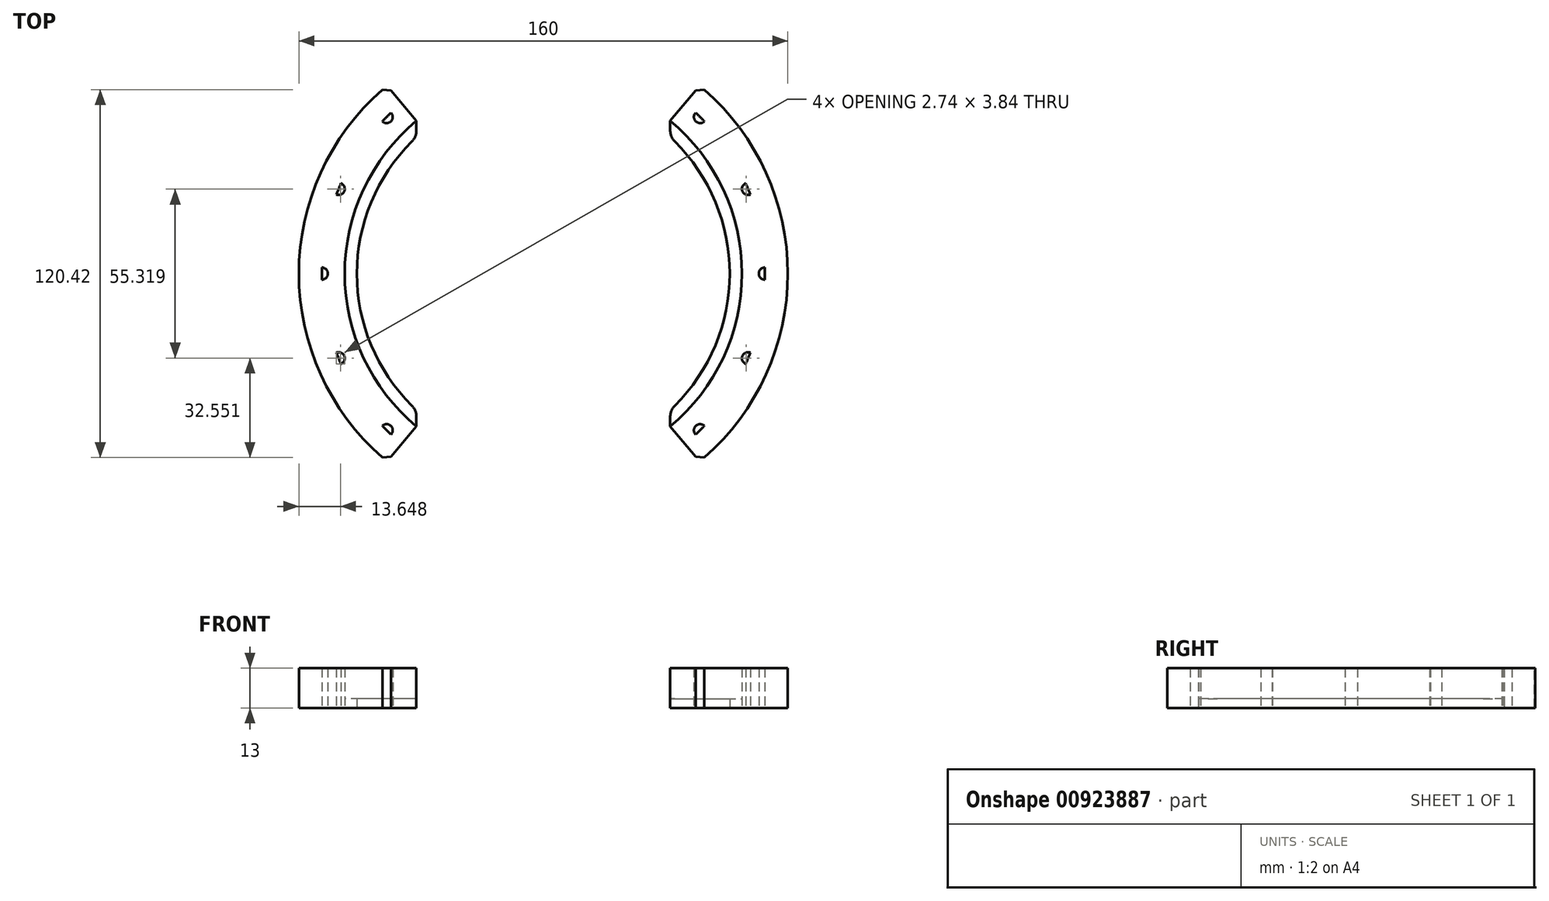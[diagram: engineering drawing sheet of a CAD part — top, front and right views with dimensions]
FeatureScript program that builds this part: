
annotation { "Feature Type Name" : "Feature", "Feature Type Description" : "" }
export const myFeature = defineFeature(function(context is Context, id is Id, definition is map)
    precondition{}
    {
        {
            var Q0;
            Q0=qCreatedBy(makeId("Top.planeOp"),FACE);
            var sketch = newSketch(context, id + "F0", { "sketchPlane" : qUnion([Q0])});
            skArc(sketch, "E0", {"start": v(-55.64, 25) * mm, "mid": v(-61, 0) * mm, "end": v(-55.64, -25) * mm});
            skArc(sketch, "E1.trimOffspring", {"start": v(55.64, -25) * mm, "mid": v(61, 0) * mm, "end": v(55.64, 25) * mm});
            skCircle(sketch, "E2", {"center": v(0, 0) * mm, "radius": 61 * mm});
            skCircle(sketch, "E3", {"center": v(0, 0) * mm, "radius": 65 * mm});
            skLineSegment(sketch, "E4", {"start": v(-41.53, 50) * mm, "end": v(-41.53, -50) * mm});
            skCircle(sketch, "E5", {"center": v(0, 0) * mm, "radius": 80 * mm});
            skLineSegment(sketch, "E6", {"start": v(-41.53, 50) * mm, "end": v(-51.12, 61.54) * mm});
            skLineSegment(sketch, "E7", {"start": v(-41.53, -50) * mm, "end": v(-51.12, -61.54) * mm});
            skArc(sketch, "E8", {"start": v(-46.33, -55.77) * mm, "mid": v(-72.5, 0) * mm, "end": v(-46.33, 55.77) * mm});
            skCircle(sketch, "E9", {"center": v(-72.5, 0) * mm, "radius": 2 * mm});
            skCircle(sketch, "E10.1.0", {"center": v(-66.98, -27.74) * mm, "radius": 2 * mm});
            skCircle(sketch, "E10.2.0", {"center": v(-51.27, -51.27) * mm, "radius": 2 * mm});
            skCircle(sketch, "E11.1.3.0", {"center": v(-27.74, -66.98) * mm, "radius": 2 * mm});
            skCircle(sketch, "E11.1.4.0", {"center": v(0, -72.5) * mm, "radius": 2 * mm});
            skCircle(sketch, "E11.1.5.0", {"center": v(27.74, -66.98) * mm, "radius": 2 * mm});
            skCircle(sketch, "E11.1.6.0", {"center": v(51.27, -51.27) * mm, "radius": 2 * mm});
            skCircle(sketch, "E11.1.7.0", {"center": v(66.98, -27.74) * mm, "radius": 2 * mm});
            skCircle(sketch, "E12.1.8.0", {"center": v(72.5, 0) * mm, "radius": 2 * mm});
            skCircle(sketch, "E12.1.9.0", {"center": v(66.98, 27.74) * mm, "radius": 2 * mm});
            skCircle(sketch, "E12.1.10.0", {"center": v(51.27, 51.27) * mm, "radius": 2 * mm});
            skCircle(sketch, "E12.1.11.0", {"center": v(27.74, 66.98) * mm, "radius": 2 * mm});
            skCircle(sketch, "E13.1.12.0", {"center": v(0, 72.5) * mm, "radius": 2 * mm});
            skCircle(sketch, "E13.1.13.0", {"center": v(-27.74, 66.98) * mm, "radius": 2 * mm});
            skCircle(sketch, "E13.1.14.0", {"center": v(-51.27, 51.27) * mm, "radius": 2 * mm});
            skCircle(sketch, "E13.1.15.0", {"center": v(-66.98, 27.74) * mm, "radius": 2 * mm});
            skSolve(sketch);
        }
        {
            var Q0;
            {var subQ0=sQuery(id+"F0.wireOp",EDGE,"E2");var subQ4=makeQuery(id+"F0.imprint","IMPRINT",VERTEX,{"disambiguationData":[OD(1.0)],"derivedFrom":subQ0});Q0=makeQuery(id+"F0.imprint","IMPRINT",FACE,{"disambiguationData":[TD([[makeQuery(id+"F0.imprint","IMPRINT",EDGE,{"disambiguationData":[TD([[subQ4,-1.0]])],"derivedFrom":subQ0}),-1.0]])]});}
            extrude(context, id + "F1", {"entities" : qUnion([Q0]), "depth" : 3 * mm, "offsetDistance" : 25 * mm});
        }
        {
            var Q0;
            {var subQ1=sQuery(id+"F0.wireOp",EDGE,"E8");var subQ8=sQuery(id+"F0.wireOp",EDGE,"E7");var subQ22=makeQuery(id+"F0.imprint","INTERSECT",VERTEX,{"derivedFrom":[subQ8,subQ1]});Q0=makeQuery(id+"F0.imprint","IMPRINT",FACE,{"disambiguationData":[TD([[makeQuery(id+"F0.imprint","IMPRINT",EDGE,{"disambiguationData":[TD([[subQ22,-1.0]])],"derivedFrom":subQ1}),-1.0]])]});}
            var Q1;
            {var subQ11=sQuery(id+"F0.wireOp",EDGE,"E6");var subQ12=sQuery(id+"F0.wireOp",EDGE,"E5");var subQ13=makeQuery(id+"F0.imprint","INTERSECT",VERTEX,{"derivedFrom":[subQ12,subQ11]});Q1=makeQuery(id+"F0.imprint","IMPRINT",FACE,{"disambiguationData":[TD([[makeQuery(id+"F0.imprint","IMPRINT",EDGE,{"disambiguationData":[TD([[subQ13,-1.0]])],"derivedFrom":subQ12}),1.0]])]});}
            extrude(context, id + "F2", {"entities" : qUnion([Q0, Q1]), "operationType" : NewBodyOperationType.ADD, "depth" : 13 * mm, "offsetDistance" : 25 * mm});
        }
        {
            var Q0;
            {var subQ0=sQuery(id+"F0.wireOp",EDGE,"E4");var subQ1=sQuery(id+"F0.wireOp",EDGE,"E2");Q0=makeQuery(id+"F1.opExtrude","SWEPT_EDGE",EDGE,{"disambiguationData":[OSD([subQ1,subQ0]),TDD([makeQuery(id+"F0.imprint","INTERSECT",VERTEX,{"disambiguationData":[OD(0.0)],"derivedFrom":[subQ1,subQ0]})])]});}
            var Q1;
            {var subQ0=sQuery(id+"F0.wireOp",EDGE,"E4");var subQ1=sQuery(id+"F0.wireOp",EDGE,"E2");Q1=makeQuery(id+"F1.opExtrude","SWEPT_EDGE",EDGE,{"disambiguationData":[OSD([subQ1,subQ0]),TDD([makeQuery(id+"F0.imprint","INTERSECT",VERTEX,{"disambiguationData":[OD(1.0)],"derivedFrom":[subQ1,subQ0]})])]});}
            fillet(context, id + "F3", {"entities" : qUnion([Q0, Q1]), "radius" : 5 * mm, "tangentPropagation" : true, "allowEdgeOverflow" : false});
        }
        {
            var Q0;
            Q0=makeQuery(id+"F2.opExtrude","SWEPT_EDGE",EDGE,{"disambiguationData":[OSD([sQuery(id+"F0.wireOp",EDGE,"E5"),sQuery(id+"F0.wireOp",EDGE,"E6")])]});
            var Q1;
            Q1=makeQuery(id+"F2.opExtrude","SWEPT_EDGE",EDGE,{"disambiguationData":[OSD([sQuery(id+"F0.wireOp",EDGE,"E5"),sQuery(id+"F0.wireOp",EDGE,"E7")])]});
            chamfer(context, id + "F4", {"entities" : qUnion([Q0, Q1]), "width" : 2 * mm, "tangentPropagation" : true});
        }
        {
            var Q0;
            Q0=makeQuery(id+"F1.opExtrude","SWEPT_BODY",BODY,{"disambiguationData":[OSD([sQuery(id+"F0.wireOp",EDGE,"E2"),sQuery(id+"F0.wireOp",EDGE,"E3"),sQuery(id+"F0.wireOp",EDGE,"E4")])]});
            var Q1;
            Q1=qCreatedBy(makeId("Right.planeOp"),FACE);
            mirror(context, id + "F5", {"entities" : qUnion([Q0]), "mirrorPlane" : qUnion([Q1])});
        }
    });
